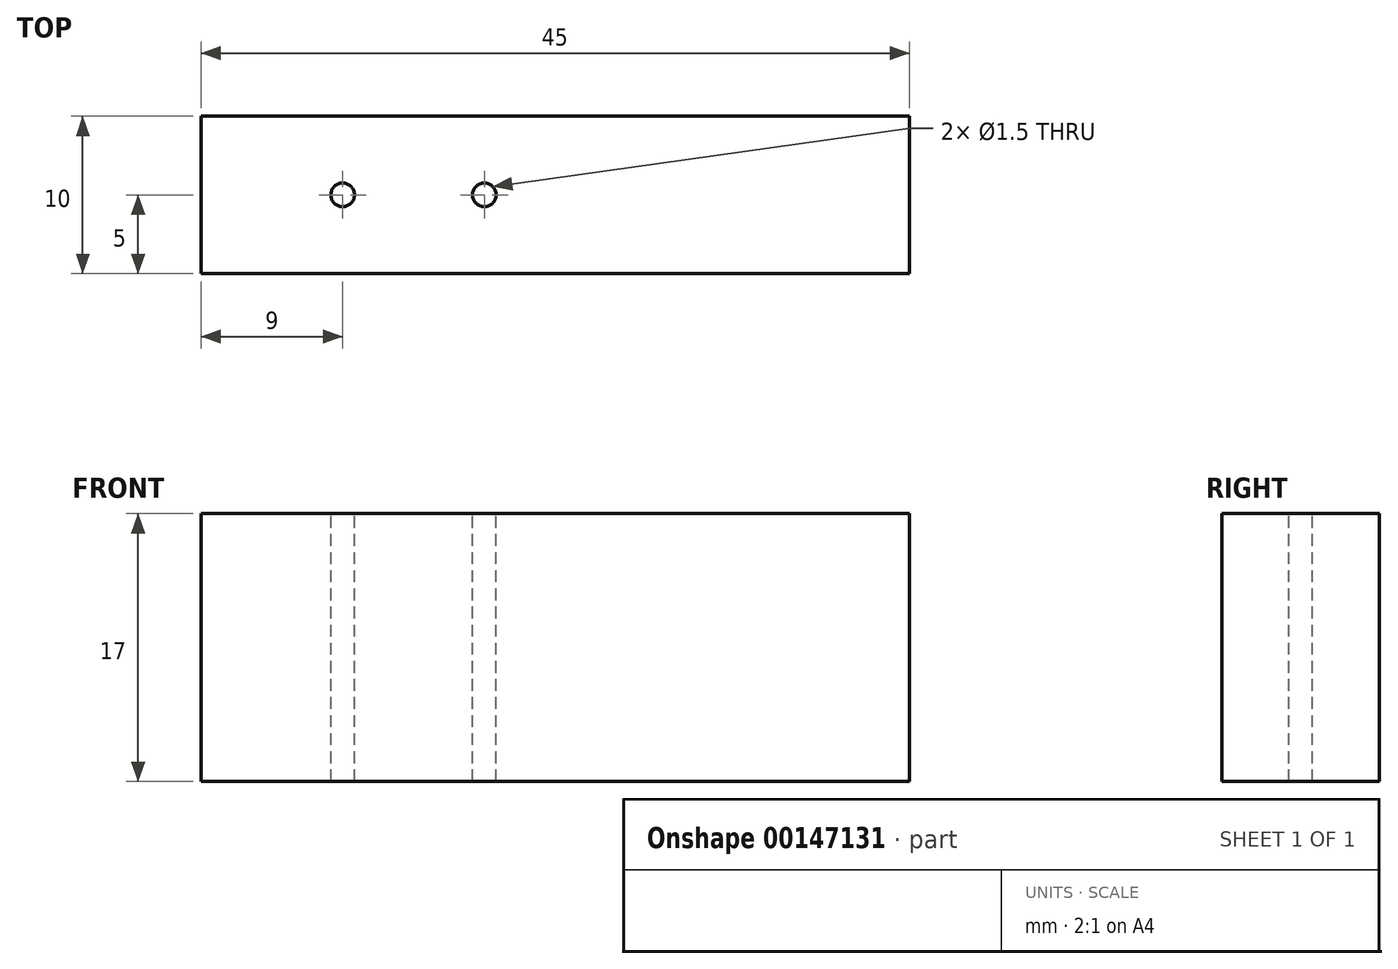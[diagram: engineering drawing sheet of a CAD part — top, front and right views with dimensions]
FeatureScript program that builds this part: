
annotation { "Feature Type Name" : "Feature", "Feature Type Description" : "" }
export const myFeature = defineFeature(function(context is Context, id is Id, definition is map)
    precondition{}
    {
        {
            var Q0;
            Q0=qCreatedBy(makeId("Top.planeOp"),FACE);
            var sketch = newSketch(context, id + "F0", { "sketchPlane" : qUnion([Q0])});
            skLineSegment(sketch, "E0.bottom", {"start": v(22.5, 5) * mm, "end": v(-22.5, 5) * mm});
            skLineSegment(sketch, "E0.top", {"start": v(22.5, -5) * mm, "end": v(-22.5, -5) * mm});
            skLineSegment(sketch, "E0.left", {"start": v(22.5, 5) * mm, "end": v(22.5, -5) * mm});
            skLineSegment(sketch, "E0.right", {"start": v(-22.5, 5) * mm, "end": v(-22.5, -5) * mm});
            skPoint(sketch, "E0.middle", {"position": v(0, 0) * mm});
            skLineSegment(sketch, "E1", {"start": v(0, 0) * mm, "end": v(4.5, 0) * mm});
            skLineSegment(sketch, "E2", {"start": v(4.5, 0) * mm, "end": v(13.5, 0) * mm});
            skCircle(sketch, "E3", {"center": v(13.5, 0) * mm, "radius": 0.75 * mm});
            skCircle(sketch, "E4", {"center": v(4.5, 0) * mm, "radius": 0.75 * mm});
            skCircle(sketch, "E5.MirrorC", {"center": v(-4.5, 0) * mm, "radius": 0.75 * mm});
            skCircle(sketch, "E6.MirrorC", {"center": v(-13.5, 0) * mm, "radius": 0.75 * mm});
            skSolve(sketch);
        }
        {
            var Q0;
            Q0=makeQuery(id+"F0.imprint","IMPRINT",FACE,{"disambiguationData":[TD([[makeQuery(id+"F0.imprint","IMPRINT",EDGE,{"derivedFrom":sQuery(id+"F0.wireOp",EDGE,"E0.bottom")}),1.0]])]});
            var Q1;
            Q1=makeQuery(id+"F0.imprint","IMPRINT",FACE,{"disambiguationData":[TD([[makeQuery(id+"F0.imprint","IMPRINT",EDGE,{"derivedFrom":sQuery(id+"F0.wireOp",EDGE,"E6.MirrorC")}),-1.0]])]});
            var Q2;
            Q2=makeQuery(id+"F0.imprint","IMPRINT",FACE,{"disambiguationData":[TD([[makeQuery(id+"F0.imprint","IMPRINT",EDGE,{"derivedFrom":sQuery(id+"F0.wireOp",EDGE,"E5.MirrorC")}),-1.0]])]});
            var Q3;
            Q3=makeQuery(id+"F0.imprint","IMPRINT",FACE,{"disambiguationData":[TD([[makeQuery(id+"F0.imprint","IMPRINT",EDGE,{"derivedFrom":sQuery(id+"F0.wireOp",EDGE,"E3")}),1.0]])]});
            var Q4;
            {var subQ0=sQuery(id+"F0.wireOp",EDGE,"E2");var subQ1=sQuery(id+"F0.wireOp",EDGE,"E1");var subQ2=makeQuery(id+"F0.imprint","INTERSECT",VERTEX,{"derivedFrom":[subQ1,subQ0]});Q4=makeQuery(id+"F0.imprint","IMPRINT",FACE,{"disambiguationData":[TD([[makeQuery(id+"F0.imprint","IMPRINT",EDGE,{"disambiguationData":[TD([[subQ2,1.0]])],"derivedFrom":subQ1}),-1.0]])]});}
            var Q5;
            {var subQ0=sQuery(id+"F0.wireOp",EDGE,"E2");var subQ1=sQuery(id+"F0.wireOp",EDGE,"E1");var subQ2=makeQuery(id+"F0.imprint","INTERSECT",VERTEX,{"derivedFrom":[subQ1,subQ0]});Q5=makeQuery(id+"F0.imprint","IMPRINT",FACE,{"disambiguationData":[TD([[makeQuery(id+"F0.imprint","IMPRINT",EDGE,{"disambiguationData":[TD([[subQ2,1.0]])],"derivedFrom":subQ1}),1.0]])]});}
            extrude(context, id + "F1", {"entities" : qUnion([Q0, Q1, Q2, Q3, Q4, Q5]), "oppositeDirection" : true, "depth" : 2 * mm});
        }
        {
            var Q0;
            Q0=makeQuery(id+"F0.imprint","IMPRINT",FACE,{"disambiguationData":[TD([[makeQuery(id+"F0.imprint","IMPRINT",EDGE,{"derivedFrom":sQuery(id+"F0.wireOp",EDGE,"E6.MirrorC")}),-1.0]])]});
            var Q1;
            Q1=makeQuery(id+"F0.imprint","IMPRINT",FACE,{"disambiguationData":[TD([[makeQuery(id+"F0.imprint","IMPRINT",EDGE,{"derivedFrom":sQuery(id+"F0.wireOp",EDGE,"E5.MirrorC")}),-1.0]])]});
            var Q2;
            {var subQ0=sQuery(id+"F0.wireOp",EDGE,"E2");var subQ1=sQuery(id+"F0.wireOp",EDGE,"E1");var subQ2=makeQuery(id+"F0.imprint","INTERSECT",VERTEX,{"derivedFrom":[subQ1,subQ0]});Q2=makeQuery(id+"F0.imprint","IMPRINT",FACE,{"disambiguationData":[TD([[makeQuery(id+"F0.imprint","IMPRINT",EDGE,{"disambiguationData":[TD([[subQ2,1.0]])],"derivedFrom":subQ1}),1.0]])]});}
            var Q3;
            {var subQ0=sQuery(id+"F0.wireOp",EDGE,"E2");var subQ1=sQuery(id+"F0.wireOp",EDGE,"E1");var subQ2=makeQuery(id+"F0.imprint","INTERSECT",VERTEX,{"derivedFrom":[subQ1,subQ0]});Q3=makeQuery(id+"F0.imprint","IMPRINT",FACE,{"disambiguationData":[TD([[makeQuery(id+"F0.imprint","IMPRINT",EDGE,{"disambiguationData":[TD([[subQ2,1.0]])],"derivedFrom":subQ1}),-1.0]])]});}
            var Q4;
            Q4=makeQuery(id+"F0.imprint","IMPRINT",FACE,{"disambiguationData":[TD([[makeQuery(id+"F0.imprint","IMPRINT",EDGE,{"derivedFrom":sQuery(id+"F0.wireOp",EDGE,"E3")}),1.0]])]});
            extrude(context, id + "F2", {"entities" : qUnion([Q0, Q1, Q2, Q3, Q4]), "operationType" : NewBodyOperationType.ADD, "depth" : 15 * mm});
        }
    });
